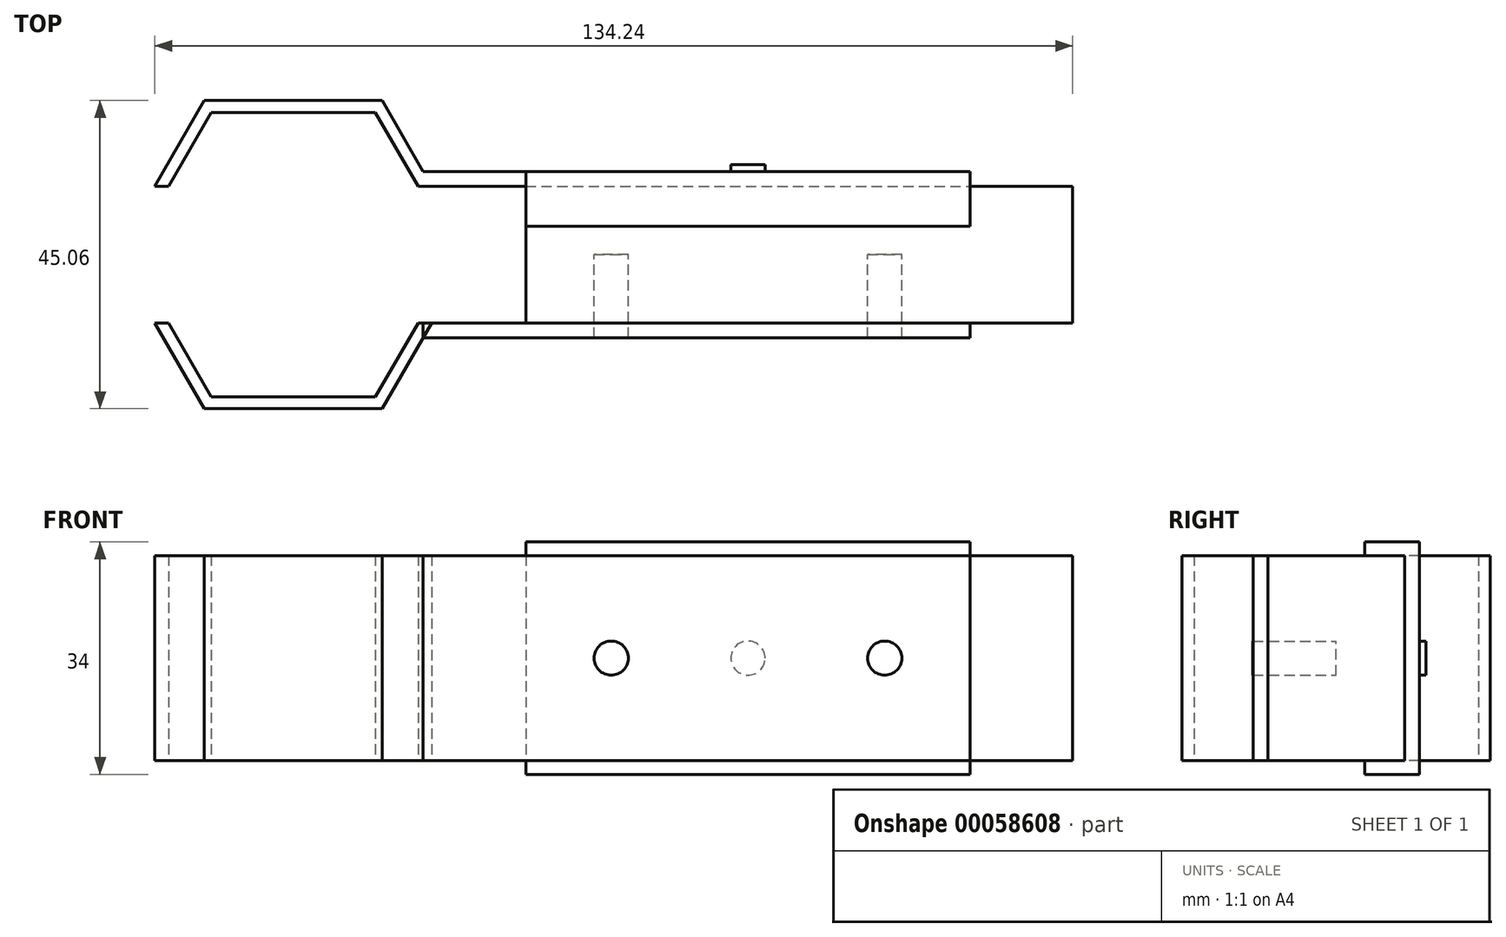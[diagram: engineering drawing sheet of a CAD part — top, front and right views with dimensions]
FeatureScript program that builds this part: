
annotation { "Feature Type Name" : "Feature", "Feature Type Description" : "" }
export const myFeature = defineFeature(function(context is Context, id is Id, definition is map)
    precondition{}
    {
        {
            var Q0;
            Q0=qCreatedBy(makeId("Top.planeOp"),FACE);
            var sketch = newSketch(context, id + "F0", { "sketchPlane" : qUnion([Q0])});
            skLineSegment(sketch, "E0.bottom", {"start": v(0, 10) * mm, "end": v(80, 10) * mm});
            skLineSegment(sketch, "E0.top", {"start": v(0, -10) * mm, "end": v(80, -10) * mm});
            skLineSegment(sketch, "E0.left", {"start": v(0, 10) * mm, "end": v(0, -10) * mm});
            skLineSegment(sketch, "E0.right", {"start": v(80, 10) * mm, "end": v(80, -10) * mm});
            skLineSegment(sketch, "E1", {"start": v(-70, 0) * mm, "end": v(98.56, 0) * mm, "construction": true});
            skSolve(sketch);
        }
        {
            var Q0;
            Q0 = qSketchRegion(id + "F0", true);
            extrude(context, id + "F1", {"entities" : qUnion([Q0]), "endBound" : BoundingType.SYMMETRIC, "depth" : 30 * mm});
        }
        {
            var Q0;
            Q0=qCreatedBy(makeId("Top.planeOp"),FACE);
            var sketch = newSketch(context, id + "F2", { "sketchPlane" : qUnion([Q0])});
            skCircle(sketch, "E2.cCircle", {"center": v(-34, 0) * mm, "radius": 20.8 * mm, "construction": true});
            skLineSegment(sketch, "E2.0", {"start": v(-9.98, 0) * mm, "end": v(-22, -20.8) * mm});
            skLineSegment(sketch, "E2.1", {"start": v(-22, -20.8) * mm, "end": v(-46, -20.8) * mm});
            skLineSegment(sketch, "E2.2", {"start": v(-46, -20.8) * mm, "end": v(-58.02, 0) * mm});
            skLineSegment(sketch, "E2.3", {"start": v(-58.02, 0) * mm, "end": v(-46, 20.8) * mm});
            skLineSegment(sketch, "E2.4", {"start": v(-46, 20.8) * mm, "end": v(-22, 20.8) * mm});
            skLineSegment(sketch, "E2.5", {"start": v(-22, 20.8) * mm, "end": v(-9.98, 0) * mm});
            skPoint(sketch, "E2.0.midPoint", {"position": v(-15.99, -10.4) * mm});
            skLineSegment(sketch, "E3", {"start": v(-34, -67.58) * mm, "end": v(-34, 63.46) * mm, "construction": true});
            skPoint(sketch, "E3.startSnap0", {"position": v(-34, 20.8) * mm});
            skPoint(sketch, "E3.endSnap0", {"position": v(-34, 20.8) * mm});
            skSolve(sketch);
        }
        {
            var Q0;
            Q0 = qSketchRegion(id + "F2", true);
            extrude(context, id + "F3", {"entities" : qUnion([Q0]), "endBound" : BoundingType.SYMMETRIC, "depth" : 100 * mm});
        }
        {
            var Q0;
            Q0=qCreatedBy(makeId("Top.planeOp"),FACE);
            var sketch = newSketch(context, id + "F4", { "sketchPlane" : qUnion([Q0])});
            skCircle(sketch, "E4.cCircle", {"center": v(-34, 0) * mm, "radius": 22.53 * mm, "construction": true});
            skLineSegment(sketch, "E4.0", {"start": v(-7.98, 0) * mm, "end": v(-21, -22.53) * mm});
            skLineSegment(sketch, "E4.1", {"start": v(-21, -22.53) * mm, "end": v(-47, -22.53) * mm});
            skLineSegment(sketch, "E4.2", {"start": v(-47, -22.53) * mm, "end": v(-60.02, 0) * mm});
            skLineSegment(sketch, "E4.3", {"start": v(-60.02, 0) * mm, "end": v(-47, 22.53) * mm});
            skLineSegment(sketch, "E4.4", {"start": v(-47, 22.53) * mm, "end": v(-21, 22.53) * mm});
            skLineSegment(sketch, "E4.5", {"start": v(-21, 22.53) * mm, "end": v(-7.98, 0) * mm});
            skPoint(sketch, "E4.0.midPoint", {"position": v(-14.49, -11.27) * mm});
            skSolve(sketch);
        }
        {
            var Q0;
            Q0 = qSketchRegion(id + "F4", true);
            extrude(context, id + "F5", {"entities" : qUnion([Q0]), "endBound" : BoundingType.SYMMETRIC, "depth" : 30 * mm});
        }
        {
            var Q0;
            Q0=makeQuery(id+"F3.opExtrude","SWEPT_BODY",BODY,{"disambiguationData":[OSD([sQuery(id+"F2.wireOp",EDGE,"E2.0"),sQuery(id+"F2.wireOp",EDGE,"E2.1"),sQuery(id+"F2.wireOp",EDGE,"E2.2"),sQuery(id+"F2.wireOp",EDGE,"E2.3"),sQuery(id+"F2.wireOp",EDGE,"E2.4"),sQuery(id+"F2.wireOp",EDGE,"E2.5")])]});
            var Q1;
            Q1=makeQuery(id+"F5.opExtrude","SWEPT_BODY",BODY,{"disambiguationData":[OSD([sQuery(id+"F4.wireOp",EDGE,"E4.0"),sQuery(id+"F4.wireOp",EDGE,"E4.1"),sQuery(id+"F4.wireOp",EDGE,"E4.2"),sQuery(id+"F4.wireOp",EDGE,"E4.3"),sQuery(id+"F4.wireOp",EDGE,"E4.4"),sQuery(id+"F4.wireOp",EDGE,"E4.5")])]});
            booleanBodies(context, id + "F6", {"operationType" : BooleanOperationType.SUBTRACTION, "tools" : qUnion([Q0]), "targets" : qUnion([Q1])});
        }
        {
            var Q0;
            Q0=qCreatedBy(makeId("Top.planeOp"),FACE);
            var sketch = newSketch(context, id + "F7", { "sketchPlane" : qUnion([Q0])});
            skLineSegment(sketch, "E5.bottom", {"start": v(65, 10) * mm, "end": v(-15, 10) * mm});
            skLineSegment(sketch, "E5.top", {"start": v(65, 12.16) * mm, "end": v(-15, 12.16) * mm});
            skLineSegment(sketch, "E5.left", {"start": v(65, 10) * mm, "end": v(65, 12.16) * mm});
            skLineSegment(sketch, "E5.right", {"start": v(-15, 10) * mm, "end": v(-15, 12.16) * mm});
            skLineSegment(sketch, "E6", {"start": v(-70.06, 0) * mm, "end": v(83.79, 0) * mm, "construction": true});
            skLineSegment(sketch, "E7.MirrorCS", {"start": v(-15, -10) * mm, "end": v(-15, -12.16) * mm});
            skLineSegment(sketch, "E8.MirrorCS", {"start": v(65, -12.16) * mm, "end": v(-15, -12.16) * mm});
            skLineSegment(sketch, "E9.MirrorCS", {"start": v(65, -10) * mm, "end": v(65, -12.16) * mm});
            skLineSegment(sketch, "E10.MirrorCS", {"start": v(65, -10) * mm, "end": v(-15, -10) * mm});
            skSolve(sketch);
        }
        {
            var Q0;
            Q0 = qSketchRegion(id + "F7", true);
            extrude(context, id + "F8", {"entities" : qUnion([Q0]), "endBound" : BoundingType.SYMMETRIC, "depth" : 30 * mm});
        }
        {
            var Q0;
            Q0=qCreatedBy(makeId("Top.planeOp"),FACE);
            var sketch = newSketch(context, id + "F9", { "sketchPlane" : qUnion([Q0])});
            skLineSegment(sketch, "E11.bottom", {"start": v(-3.86, 10) * mm, "end": v(-17.92, 10) * mm});
            skLineSegment(sketch, "E11.top", {"start": v(-3.86, -10) * mm, "end": v(-17.92, -10) * mm});
            skLineSegment(sketch, "E11.left", {"start": v(-3.86, 10) * mm, "end": v(-3.86, -10) * mm});
            skLineSegment(sketch, "E11.right", {"start": v(-17.92, 10) * mm, "end": v(-17.92, -10) * mm});
            skLineSegment(sketch, "E12", {"start": v(-34.94, 33.87) * mm, "end": v(-34.94, -36.08) * mm, "construction": true});
            skSolve(sketch);
        }
        {
            var Q0;
            Q0 = qSketchRegion(id + "F9", true);
            extrude(context, id + "F10", {"entities" : qUnion([Q0]), "endBound" : BoundingType.SYMMETRIC, "depth" : 40 * mm});
        }
        {
            var Q0;
            Q0=makeQuery(id+"F10.opExtrude","SWEPT_BODY",BODY,{"disambiguationData":[OSD([sQuery(id+"F9.wireOp",EDGE,"E11.bottom"),sQuery(id+"F9.wireOp",EDGE,"E11.top"),sQuery(id+"F9.wireOp",EDGE,"E11.left"),sQuery(id+"F9.wireOp",EDGE,"E11.right")])]});
            var Q1;
            Q1=makeQuery(id+"F5.opExtrude","SWEPT_BODY",BODY,{"disambiguationData":[OSD([sQuery(id+"F4.wireOp",EDGE,"E4.0"),sQuery(id+"F4.wireOp",EDGE,"E4.1"),sQuery(id+"F4.wireOp",EDGE,"E4.2"),sQuery(id+"F4.wireOp",EDGE,"E4.3"),sQuery(id+"F4.wireOp",EDGE,"E4.4"),sQuery(id+"F4.wireOp",EDGE,"E4.5")])]});
            booleanBodies(context, id + "F11", {"operationType" : BooleanOperationType.SUBTRACTION, "tools" : qUnion([Q0]), "targets" : qUnion([Q1])});
        }
        {
            var Q0;
            Q0=qCreatedBy(makeId("Top.planeOp"),FACE);
            var sketch = newSketch(context, id + "F12", { "sketchPlane" : qUnion([Q0])});
            skLineSegment(sketch, "E13.rect.bottom", {"start": v(-70.33, 10) * mm, "end": v(-30.33, 10) * mm});
            skLineSegment(sketch, "E13.rect.top", {"start": v(-70.33, -10) * mm, "end": v(-30.33, -10) * mm});
            skLineSegment(sketch, "E13.rect.left", {"start": v(-70.33, 10) * mm, "end": v(-70.33, -10) * mm});
            skLineSegment(sketch, "E13.rect.right", {"start": v(-30.33, 10) * mm, "end": v(-30.33, -10) * mm});
            skPoint(sketch, "E13.rect.middle", {"position": v(-50.33, 0) * mm});
            skSolve(sketch);
        }
        {
            var Q0;
            Q0 = qSketchRegion(id + "F12", true);
            extrude(context, id + "F13", {"entities" : qUnion([Q0]), "endBound" : BoundingType.SYMMETRIC, "depth" : 30 * mm});
        }
        {
            var Q0;
            Q0=makeQuery(id+"F13.opExtrude","SWEPT_BODY",BODY,{"disambiguationData":[OSD([sQuery(id+"F12.wireOp",EDGE,"E13.rect.bottom"),sQuery(id+"F12.wireOp",EDGE,"E13.rect.top"),sQuery(id+"F12.wireOp",EDGE,"E13.rect.left"),sQuery(id+"F12.wireOp",EDGE,"E13.rect.right")])]});
            var Q1;
            Q1=makeQuery(id+"F5.opExtrude","SWEPT_BODY",BODY,{"disambiguationData":[OSD([sQuery(id+"F4.wireOp",EDGE,"E4.0"),sQuery(id+"F4.wireOp",EDGE,"E4.1"),sQuery(id+"F4.wireOp",EDGE,"E4.2"),sQuery(id+"F4.wireOp",EDGE,"E4.3"),sQuery(id+"F4.wireOp",EDGE,"E4.4"),sQuery(id+"F4.wireOp",EDGE,"E4.5")])]});
            booleanBodies(context, id + "F14", {"operationType" : BooleanOperationType.SUBTRACTION, "tools" : qUnion([Q0]), "targets" : qUnion([Q1])});
        }
        {
            var Q0;
            Q0=makeQuery(id+"F14.opBoolean","SPLIT",BODY,{"disambiguationData":[OD(1.0)],"derivedFrom":makeQuery(id+"F5.opExtrude","SWEPT_BODY",BODY,{"disambiguationData":[OSD([sQuery(id+"F4.wireOp",EDGE,"E4.0"),sQuery(id+"F4.wireOp",EDGE,"E4.1"),sQuery(id+"F4.wireOp",EDGE,"E4.2"),sQuery(id+"F4.wireOp",EDGE,"E4.3"),sQuery(id+"F4.wireOp",EDGE,"E4.4"),sQuery(id+"F4.wireOp",EDGE,"E4.5")])]})});
            var Q1;
            Q1=makeQuery(id+"F8.opExtrude","SWEPT_BODY",BODY,{"disambiguationData":[OSD([sQuery(id+"F7.wireOp",EDGE,"E5.bottom"),sQuery(id+"F7.wireOp",EDGE,"E5.top"),sQuery(id+"F7.wireOp",EDGE,"E5.left"),sQuery(id+"F7.wireOp",EDGE,"E5.right")])]});
            booleanBodies(context, id + "F15", {"operationType" : BooleanOperationType.UNION, "tools" : qUnion([Q0, Q1])});
        }
        {
            var Q0;
            Q0=qCreatedBy(makeId("Front.planeOp"),FACE);
            var sketch = newSketch(context, id + "F16", { "sketchPlane" : qUnion([Q0])});
            skCircle(sketch, "E14", {"center": v(12.5, 0) * mm, "radius": 2.5 * mm});
            skCircle(sketch, "E15", {"center": v(52.5, 0) * mm, "radius": 2.5 * mm});
            skLineSegment(sketch, "E16", {"start": v(32.5, 48.27) * mm, "end": v(32.5, -34) * mm, "construction": true});
            skSolve(sketch);
        }
        {
            var Q0;
            Q0 = qSketchRegion(id + "F16", true);
            extrude(context, id + "F17", {"entities" : qUnion([Q0]), "depth" : 12.2 * mm});
        }
        {
            var Q0;
            Q0=makeQuery(id+"F1.opExtrude","CAP_FACE",FACE,{"disambiguationData":[OSD([sQuery(id+"F0.wireOp",EDGE,"E0.bottom"),sQuery(id+"F0.wireOp",EDGE,"E0.top"),sQuery(id+"F0.wireOp",EDGE,"E0.left"),sQuery(id+"F0.wireOp",EDGE,"E0.right")])],"isStart":false});
            cPlane(context, id + "F18", {"entities" : qUnion([Q0]), "cplaneType" : CPlaneType.OFFSET, "offset" : 0 * mm, "width" : 150 * mm, "height" : 150 * mm});
        }
        {
            var Q0;
            Q0=qCreatedBy(id+"F18.planeOp",FACE);
            var sketch = newSketch(context, id + "F19", { "sketchPlane" : qUnion([Q0])});
            skLineSegment(sketch, "E17.bottom", {"start": v(0, 12.16) * mm, "end": v(65, 12.16) * mm});
            skLineSegment(sketch, "E17.top", {"start": v(0, 4.16) * mm, "end": v(65, 4.16) * mm});
            skLineSegment(sketch, "E17.left", {"start": v(0, 12.16) * mm, "end": v(0, 4.16) * mm});
            skLineSegment(sketch, "E17.right", {"start": v(65, 12.16) * mm, "end": v(65, 4.16) * mm});
            skSolve(sketch);
        }
        {
            var Q0;
            Q0=makeQuery(id+"F19.imprint","IMPRINT",FACE,{"disambiguationData":[TD([[makeQuery(id+"F19.imprint","IMPRINT",EDGE,{"derivedFrom":sQuery(id+"F19.wireOp",EDGE,"E17.bottom")}),-1.0]])]});
            extrude(context, id + "F20", {"entities" : qUnion([Q0]), "depth" : 2 * mm});
        }
        {
            var Q0;
            {var subQ0=sQuery(id+"F4.wireOp",EDGE,"E4.5");var subQ1=sQuery(id+"F4.wireOp",EDGE,"E4.4");var subQ2=sQuery(id+"F4.wireOp",EDGE,"E4.3");Q0=makeQuery(id+"F15.opBoolean","MERGE",FACE,{"derivedFrom":[makeQuery(id+"F8.opExtrude","CAP_FACE",FACE,{"disambiguationData":[OSD([sQuery(id+"F7.wireOp",EDGE,"E5.bottom"),sQuery(id+"F7.wireOp",EDGE,"E5.top"),sQuery(id+"F7.wireOp",EDGE,"E5.left"),sQuery(id+"F7.wireOp",EDGE,"E5.right")])],"isStart":true}),makeQuery(id+"F14.opBoolean","SPLIT",FACE,{"disambiguationData":[TD([makeQuery(id+"F5.opExtrude","SWEPT_FACE",FACE,{"disambiguationData":[OSD([subQ2])]})])],"derivedFrom":makeQuery(id+"F5.opExtrude","CAP_FACE",FACE,{"disambiguationData":[OSD([sQuery(id+"F4.wireOp",EDGE,"E4.0"),sQuery(id+"F4.wireOp",EDGE,"E4.1"),sQuery(id+"F4.wireOp",EDGE,"E4.2"),subQ2,subQ1,subQ0])],"isStart":true})})]});}
            cPlane(context, id + "F21", {"entities" : qUnion([Q0]), "cplaneType" : CPlaneType.OFFSET, "offset" : 0 * mm, "width" : 150 * mm, "height" : 150 * mm});
        }
        {
            var Q0;
            Q0=qCreatedBy(id+"F21.planeOp",FACE);
            var sketch = newSketch(context, id + "F22", { "sketchPlane" : qUnion([Q0])});
            skLineSegment(sketch, "E18.bottom", {"start": v(0, -12.16) * mm, "end": v(65, -12.16) * mm});
            skLineSegment(sketch, "E18.top", {"start": v(0, -4.16) * mm, "end": v(65, -4.16) * mm});
            skLineSegment(sketch, "E18.left", {"start": v(0, -12.16) * mm, "end": v(0, -4.16) * mm});
            skLineSegment(sketch, "E18.right", {"start": v(65, -12.16) * mm, "end": v(65, -4.16) * mm});
            skSolve(sketch);
        }
        {
            var Q0;
            Q0=makeQuery(id+"F22.imprint","IMPRINT",FACE,{"disambiguationData":[TD([[makeQuery(id+"F22.imprint","IMPRINT",EDGE,{"derivedFrom":sQuery(id+"F22.wireOp",EDGE,"E18.bottom")}),1.0]])]});
            extrude(context, id + "F23", {"entities" : qUnion([Q0]), "depth" : 2 * mm});
        }
        {
            var Q0;
            Q0=makeQuery(id+"F23.opExtrude","SWEPT_BODY",BODY,{"disambiguationData":[OSD([sQuery(id+"F22.wireOp",EDGE,"E18.bottom"),sQuery(id+"F22.wireOp",EDGE,"E18.top"),sQuery(id+"F22.wireOp",EDGE,"E18.left"),sQuery(id+"F22.wireOp",EDGE,"E18.right")])]});
            var Q1;
            Q1=makeQuery(id+"F20.opExtrude","SWEPT_BODY",BODY,{"disambiguationData":[OSD([sQuery(id+"F19.wireOp",EDGE,"E17.bottom"),sQuery(id+"F19.wireOp",EDGE,"E17.top"),sQuery(id+"F19.wireOp",EDGE,"E17.left"),sQuery(id+"F19.wireOp",EDGE,"E17.right")])]});
            var Q2;
            Q2=makeQuery(id+"F14.opBoolean","SPLIT",BODY,{"disambiguationData":[OD(1.0)],"derivedFrom":makeQuery(id+"F5.opExtrude","SWEPT_BODY",BODY,{"disambiguationData":[OSD([sQuery(id+"F4.wireOp",EDGE,"E4.0"),sQuery(id+"F4.wireOp",EDGE,"E4.1"),sQuery(id+"F4.wireOp",EDGE,"E4.2"),sQuery(id+"F4.wireOp",EDGE,"E4.3"),sQuery(id+"F4.wireOp",EDGE,"E4.4"),sQuery(id+"F4.wireOp",EDGE,"E4.5")])]})});
            booleanBodies(context, id + "F24", {"operationType" : BooleanOperationType.UNION, "tools" : qUnion([Q0, Q1, Q2])});
        }
        {
            var Q0;
            Q0=makeQuery(id+"F24.opBoolean","MERGE",FACE,{"derivedFrom":[makeQuery(id+"F8.opExtrude","SWEPT_FACE",FACE,{"disambiguationData":[OSD([sQuery(id+"F7.wireOp",EDGE,"E5.top")])]}),makeQuery(id+"F20.opExtrude","SWEPT_FACE",FACE,{"disambiguationData":[OSD([sQuery(id+"F19.wireOp",EDGE,"E17.bottom")])]}),makeQuery(id+"F23.opExtrude","SWEPT_FACE",FACE,{"disambiguationData":[OSD([sQuery(id+"F22.wireOp",EDGE,"E18.bottom")])]})]});
            var sketch = newSketch(context, id + "F25", { "sketchPlane" : qUnion([Q0])});
            skCircle(sketch, "E19", {"center": v(-32.5, 0) * mm, "radius": 2.5 * mm});
            skSolve(sketch);
        }
        {
            var Q0;
            Q0=makeQuery(id+"F25.imprint","IMPRINT",FACE,{"disambiguationData":[TD([[makeQuery(id+"F25.imprint","IMPRINT",EDGE,{"derivedFrom":sQuery(id+"F25.wireOp",EDGE,"E19")}),1.0]])]});
            extrude(context, id + "F26", {"entities" : qUnion([Q0]), "depth" : 1 * mm});
        }
    });
